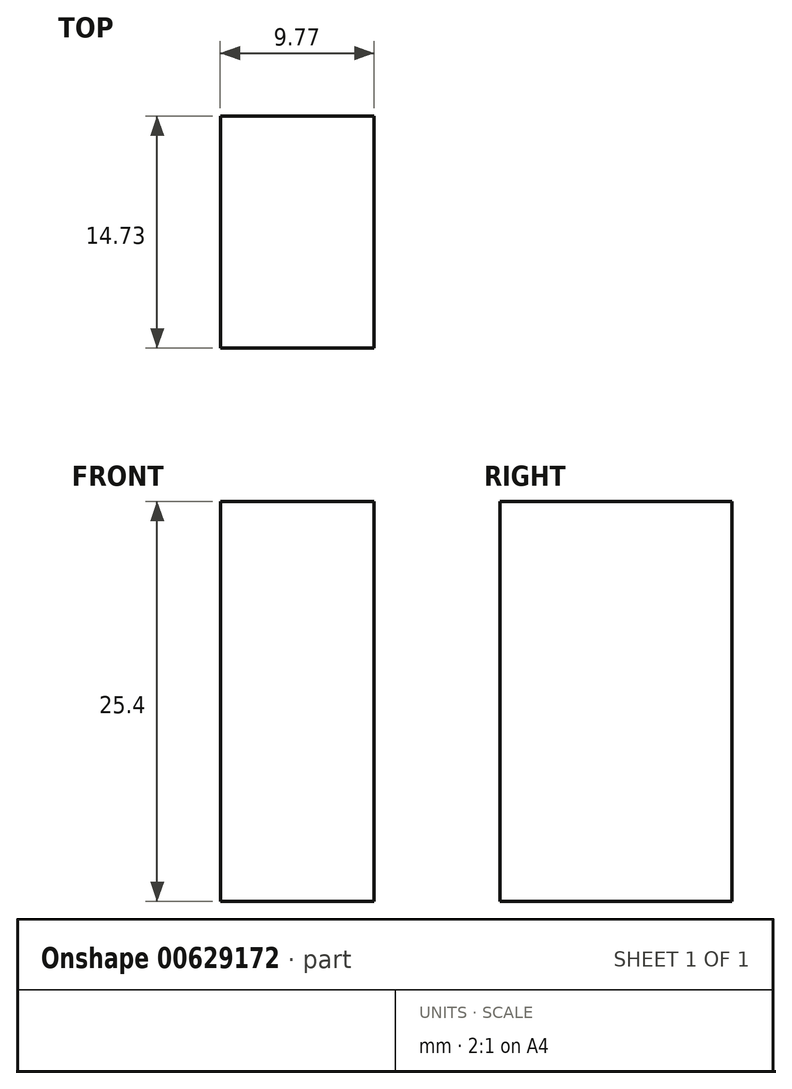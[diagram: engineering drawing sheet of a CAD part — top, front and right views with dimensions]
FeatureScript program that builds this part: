
annotation { "Feature Type Name" : "Feature", "Feature Type Description" : "" }
export const myFeature = defineFeature(function(context is Context, id is Id, definition is map)
    precondition{}
    {
        {
            var Q0;
            Q0=qCreatedBy(makeId("Top.planeOp"),FACE);
            var sketch = newSketch(context, id + "F0", { "sketchPlane" : qUnion([Q0])});
            skLineSegment(sketch, "E0.bottom", {"start": v(91.9, 48.46) * mm, "end": v(101.67, 48.46) * mm});
            skLineSegment(sketch, "E0.top", {"start": v(91.9, 33.73) * mm, "end": v(101.67, 33.73) * mm});
            skLineSegment(sketch, "E0.left", {"start": v(91.9, 48.46) * mm, "end": v(91.9, 33.73) * mm});
            skLineSegment(sketch, "E0.right", {"start": v(101.67, 48.46) * mm, "end": v(101.67, 33.73) * mm});
            skSolve(sketch);
        }
        {
            var Q0;
            Q0=makeQuery(id+"F0.imprint","IMPRINT",FACE,{"disambiguationData":[TD([[makeQuery(id+"F0.imprint","IMPRINT",EDGE,{"derivedFrom":sQuery(id+"F0.wireOp",EDGE,"E0.bottom")}),-1.0]])]});
            extrude(context, id + "F1", {"entities" : qUnion([Q0]), "depth" : 25.4 * mm, "offsetDistance" : 25.4 * mm});
        }
    });
